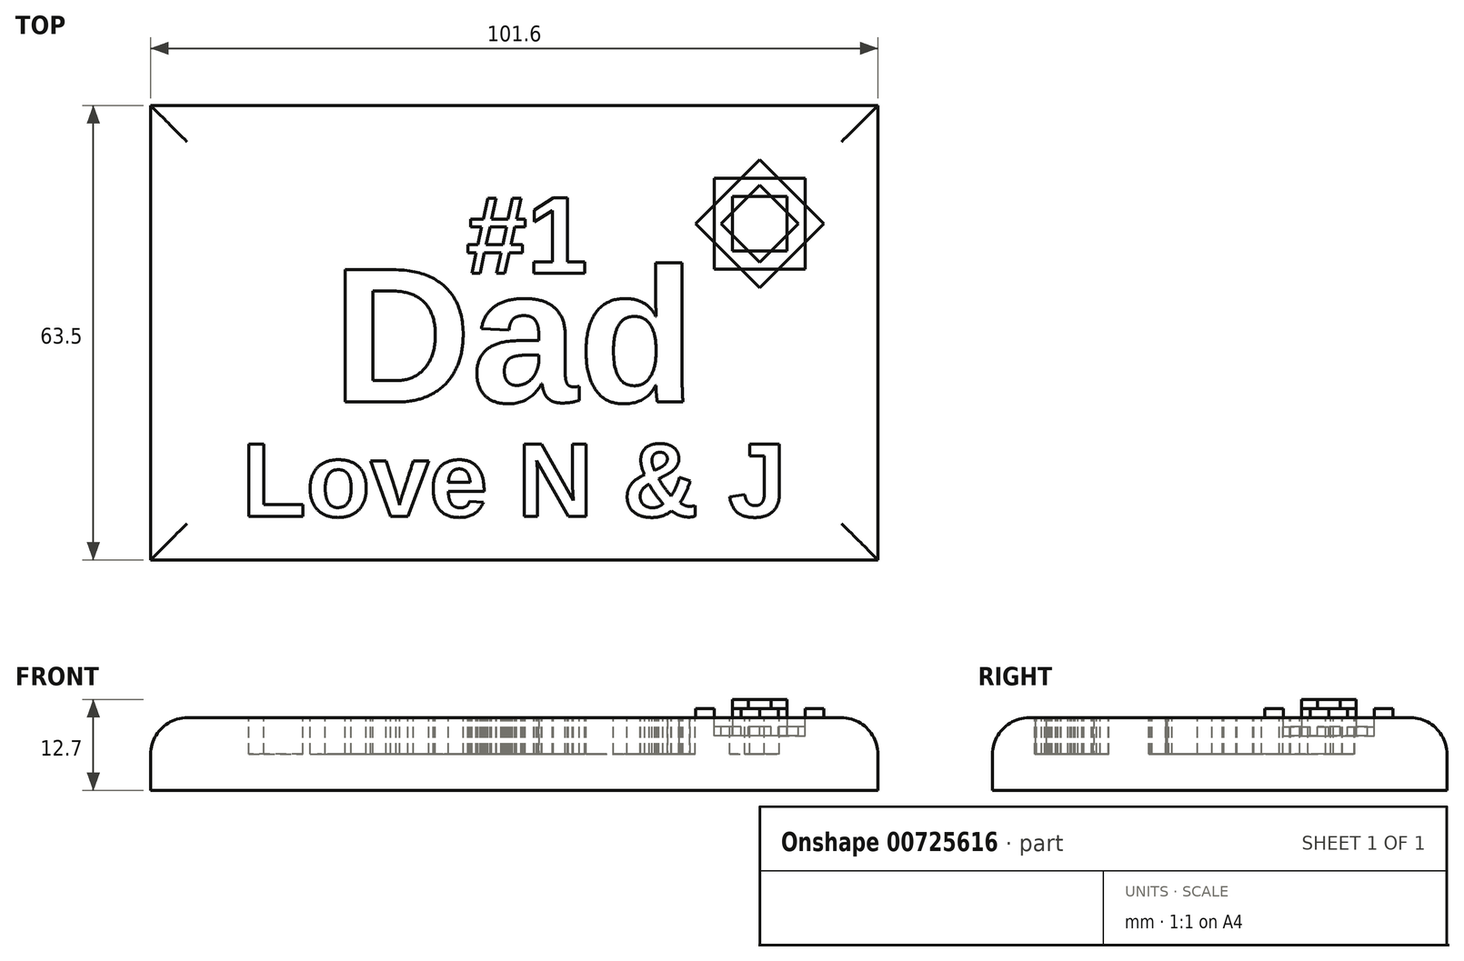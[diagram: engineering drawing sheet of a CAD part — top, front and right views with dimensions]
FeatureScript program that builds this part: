
annotation { "Feature Type Name" : "Feature", "Feature Type Description" : "" }
export const myFeature = defineFeature(function(context is Context, id is Id, definition is map)
    precondition{}
    {
        {
            var Q0;
            Q0=qCreatedBy(makeId("Top.planeOp"),FACE);
            var sketch = newSketch(context, id + "F0", { "sketchPlane" : qUnion([Q0])});
            skLineSegment(sketch, "E0.bottom", {"start": v(-50.8, 46.81) * mm, "end": v(50.8, 46.81) * mm});
            skLineSegment(sketch, "E0.top", {"start": v(-50.8, -16.69) * mm, "end": v(50.8, -16.69) * mm});
            skLineSegment(sketch, "E0.left", {"start": v(-50.8, 46.81) * mm, "end": v(-50.8, -16.69) * mm});
            skLineSegment(sketch, "E0.right", {"start": v(50.8, 46.81) * mm, "end": v(50.8, -16.69) * mm});
            skLineSegment(sketch, "E1", {"start": v(0, 46.81) * mm, "end": v(0, -16.69) * mm, "construction": true});
            skPoint(sketch, "E2", {"position": v(0, 15.06) * mm});
            skSolve(sketch);
        }
        {
            var Q0;
            Q0=qSketchRegion(id+"F0",true);
            extrude(context, id + "F1", {"entities" : qUnion([Q0]), "depth" : 10.16 * mm, "offsetDistance" : 25.4 * mm});
        }
        {
            var Q0;
            Q0=makeQuery(id+"F1.opExtrude","CAP_EDGE",EDGE,{"disambiguationData":[OSD([sQuery(id+"F0.wireOp",EDGE,"E0.left")])],"isStart":false});
            var Q1;
            Q1=makeQuery(id+"F1.opExtrude","CAP_EDGE",EDGE,{"disambiguationData":[OSD([sQuery(id+"F0.wireOp",EDGE,"E0.bottom")])],"isStart":false});
            var Q2;
            Q2=makeQuery(id+"F1.opExtrude","CAP_EDGE",EDGE,{"disambiguationData":[OSD([sQuery(id+"F0.wireOp",EDGE,"E0.right")])],"isStart":false});
            var Q3;
            Q3=makeQuery(id+"F1.opExtrude","CAP_EDGE",EDGE,{"disambiguationData":[OSD([sQuery(id+"F0.wireOp",EDGE,"E0.top")])],"isStart":false});
            fillet(context, id + "F2", {"entities" : qUnion([Q0, Q1, Q2, Q3]), "radius" : 5.08 * mm, "tangentPropagation" : true, "allowEdgeOverflow" : false});
        }
        {
            var Q0;
            Q0=makeQuery(id+"F1.opExtrude","CAP_FACE",FACE,{"disambiguationData":[OSD([sQuery(id+"F0.wireOp",EDGE,"E0.bottom"),sQuery(id+"F0.wireOp",EDGE,"E0.top"),sQuery(id+"F0.wireOp",EDGE,"E0.left"),sQuery(id+"F0.wireOp",EDGE,"E0.right")])],"isStart":false});
            var sketch = newSketch(context, id + "F3", { "sketchPlane" : qUnion([Q0])});
            skText(sketch, "E3", { "text": "Dad", "fontName": "Arimo-Bold.ttf"});
            skPoint(sketch, "E4", {"position": v(0, 15.06) * mm});
            skText(sketch, "E5", { "text": "#1", "fontName": "Arimo-Bold.ttf"});
            skText(sketch, "E6", { "text": "Love N & J", "fontName": "Arimo-Bold.ttf"});
            skPoint(sketch, "E7", {"position": v(0, -5.3) * mm});
            const initialGuessF3  = {"E3": [-0.0254, 0.0054, 1, 0, 0.01933], "E5": [-0.00674, 0.0234, 1, 0, 0.01102], "E6": [-0.0381, -0.01061, 1, 0, 0.01061]};
            skSetInitialGuess(sketch, initialGuessF3);
            skSolve(sketch);
        }
        {
            var Q0;
            Q0 = qSketchRegion(id + "F3", true);
            extrude(context, id + "F4", {"entities" : qUnion([Q0]), "operationType" : NewBodyOperationType.REMOVE, "oppositeDirection" : true, "depth" : 5.08 * mm, "offsetDistance" : 25.4 * mm});
        }
        {
            var Q0;
            {var subQ0=sQuery(id+"F0.wireOp",EDGE,"E0.right");var subQ1=sQuery(id+"F0.wireOp",EDGE,"E0.left");var subQ2=sQuery(id+"F0.wireOp",EDGE,"E0.top");var subQ3=sQuery(id+"F0.wireOp",EDGE,"E0.bottom");Q0=makeQuery(id+"F4.boolean.opBoolean","SPLIT",FACE,{"disambiguationData":[TD([makeQuery(id+"F2.opFillet","BLEND_FACE",FACE,{"disambiguationData":[OSD([subQ3])]})])],"derivedFrom":makeQuery(id+"F1.opExtrude","CAP_FACE",FACE,{"disambiguationData":[OSD([subQ3,subQ2,subQ1,subQ0])],"isStart":false})});}
            var sketch = newSketch(context, id + "F5", { "sketchPlane" : qUnion([Q0])});
            skLineSegment(sketch, "E8.bottom", {"start": v(40.64, 23.95) * mm, "end": v(27.94, 23.95) * mm});
            skLineSegment(sketch, "E8.top", {"start": v(40.64, 36.65) * mm, "end": v(27.94, 36.65) * mm});
            skLineSegment(sketch, "E8.left", {"start": v(40.64, 23.95) * mm, "end": v(40.64, 36.65) * mm});
            skLineSegment(sketch, "E8.right", {"start": v(27.94, 23.95) * mm, "end": v(27.94, 36.65) * mm});
            skPoint(sketch, "E8.middle", {"position": v(34.29, 30.3) * mm});
            skLineSegment(sketch, "E9.bottom", {"start": v(34.29, 21.32) * mm, "end": v(43.27, 30.3) * mm});
            skLineSegment(sketch, "E9.top", {"start": v(25.3, 30.3) * mm, "end": v(34.29, 39.28) * mm});
            skLineSegment(sketch, "E9.left", {"start": v(34.29, 21.32) * mm, "end": v(25.3, 30.3) * mm});
            skLineSegment(sketch, "E9.right", {"start": v(43.27, 30.3) * mm, "end": v(34.29, 39.28) * mm});
            skLineSegment(sketch, "E10.bottom", {"start": v(38.1, 34.11) * mm, "end": v(30.48, 34.11) * mm});
            skLineSegment(sketch, "E10.top", {"start": v(38.1, 26.5) * mm, "end": v(30.48, 26.5) * mm});
            skLineSegment(sketch, "E10.left", {"start": v(38.1, 34.11) * mm, "end": v(38.1, 26.5) * mm});
            skLineSegment(sketch, "E10.right", {"start": v(30.48, 34.11) * mm, "end": v(30.48, 26.5) * mm});
            skLineSegment(sketch, "E11.bottom", {"start": v(39.68, 30.3) * mm, "end": v(34.29, 35.7) * mm});
            skLineSegment(sketch, "E11.top", {"start": v(34.29, 24.92) * mm, "end": v(28.9, 30.3) * mm});
            skLineSegment(sketch, "E11.left", {"start": v(39.68, 30.3) * mm, "end": v(34.29, 24.92) * mm});
            skLineSegment(sketch, "E11.right", {"start": v(34.29, 35.7) * mm, "end": v(28.9, 30.3) * mm});
            skSolve(sketch);
        }
        {
            var Q0;
            {var subQ0=sQuery(id+"F5.wireOp",EDGE,"E9.right");var subQ1=sQuery(id+"F5.wireOp",EDGE,"E8.top");var subQ2=makeQuery(id+"F5.imprint","INTERSECT",VERTEX,{"derivedFrom":[subQ1,subQ0]});Q0=makeQuery(id+"F5.imprint","IMPRINT",FACE,{"disambiguationData":[TD([[makeQuery(id+"F5.imprint","IMPRINT",EDGE,{"disambiguationData":[TD([[subQ2,-1.0]])],"derivedFrom":subQ1}),-1.0]])]});}
            var Q1;
            {var subQ0=sQuery(id+"F5.wireOp",EDGE,"E9.left");var subQ1=sQuery(id+"F5.wireOp",EDGE,"E8.right");var subQ2=makeQuery(id+"F5.imprint","INTERSECT",VERTEX,{"derivedFrom":[subQ1,subQ0]});Q1=makeQuery(id+"F5.imprint","IMPRINT",FACE,{"disambiguationData":[TD([[makeQuery(id+"F5.imprint","IMPRINT",EDGE,{"disambiguationData":[TD([[subQ2,-1.0]])],"derivedFrom":subQ1}),1.0]])]});}
            var Q2;
            {var subQ0=sQuery(id+"F5.wireOp",EDGE,"E9.bottom");var subQ1=sQuery(id+"F5.wireOp",EDGE,"E8.bottom");var subQ2=makeQuery(id+"F5.imprint","INTERSECT",VERTEX,{"derivedFrom":[subQ1,subQ0]});Q2=makeQuery(id+"F5.imprint","IMPRINT",FACE,{"disambiguationData":[TD([[makeQuery(id+"F5.imprint","IMPRINT",EDGE,{"disambiguationData":[TD([[subQ2,-1.0]])],"derivedFrom":subQ1}),1.0]])]});}
            var Q3;
            {var subQ0=sQuery(id+"F5.wireOp",EDGE,"E9.bottom");var subQ1=sQuery(id+"F5.wireOp",EDGE,"E8.left");var subQ2=makeQuery(id+"F5.imprint","INTERSECT",VERTEX,{"derivedFrom":[subQ1,subQ0]});Q3=makeQuery(id+"F5.imprint","IMPRINT",FACE,{"disambiguationData":[TD([[makeQuery(id+"F5.imprint","IMPRINT",EDGE,{"disambiguationData":[TD([[subQ2,-1.0]])],"derivedFrom":subQ1}),-1.0]])]});}
            var Q4;
            {var subQ0=sQuery(id+"F5.wireOp",EDGE,"E10.left");var subQ1=sQuery(id+"F5.wireOp",EDGE,"E10.top");var subQ2=makeQuery(id+"F5.imprint","INTERSECT",VERTEX,{"derivedFrom":[subQ1,subQ0]});Q4=makeQuery(id+"F5.imprint","IMPRINT",FACE,{"disambiguationData":[TD([[makeQuery(id+"F5.imprint","IMPRINT",EDGE,{"disambiguationData":[TD([[subQ2,-1.0]])],"derivedFrom":subQ1}),-1.0]])]});}
            var Q5;
            {var subQ0=sQuery(id+"F5.wireOp",EDGE,"E10.right");var subQ1=sQuery(id+"F5.wireOp",EDGE,"E10.top");var subQ2=makeQuery(id+"F5.imprint","INTERSECT",VERTEX,{"derivedFrom":[subQ1,subQ0]});Q5=makeQuery(id+"F5.imprint","IMPRINT",FACE,{"disambiguationData":[TD([[makeQuery(id+"F5.imprint","IMPRINT",EDGE,{"disambiguationData":[TD([[subQ2,1.0]])],"derivedFrom":subQ1}),-1.0]])]});}
            var Q6;
            {var subQ0=sQuery(id+"F5.wireOp",EDGE,"E10.right");var subQ1=sQuery(id+"F5.wireOp",EDGE,"E10.bottom");var subQ2=makeQuery(id+"F5.imprint","INTERSECT",VERTEX,{"derivedFrom":[subQ1,subQ0]});Q6=makeQuery(id+"F5.imprint","IMPRINT",FACE,{"disambiguationData":[TD([[makeQuery(id+"F5.imprint","IMPRINT",EDGE,{"disambiguationData":[TD([[subQ2,1.0]])],"derivedFrom":subQ1}),1.0]])]});}
            var Q7;
            {var subQ0=sQuery(id+"F5.wireOp",EDGE,"E10.left");var subQ1=sQuery(id+"F5.wireOp",EDGE,"E10.bottom");var subQ2=makeQuery(id+"F5.imprint","INTERSECT",VERTEX,{"derivedFrom":[subQ1,subQ0]});Q7=makeQuery(id+"F5.imprint","IMPRINT",FACE,{"disambiguationData":[TD([[makeQuery(id+"F5.imprint","IMPRINT",EDGE,{"disambiguationData":[TD([[subQ2,-1.0]])],"derivedFrom":subQ1}),1.0]])]});}
            extrude(context, id + "F6", {"entities" : qUnion([Q0, Q1, Q2, Q3, Q4, Q5, Q6, Q7]), "operationType" : NewBodyOperationType.ADD, "depth" : 1.27 * mm, "offsetDistance" : 25.4 * mm});
        }
        {
            var Q0;
            {var subQ5=sQuery(id+"F5.wireOp",EDGE,"E11.bottom");var subQ13=sQuery(id+"F5.wireOp",EDGE,"E10.bottom");var subQ14=makeQuery(id+"F5.imprint","INTERSECT",VERTEX,{"derivedFrom":[subQ13,subQ5]});Q0=makeQuery(id+"F5.imprint","IMPRINT",FACE,{"disambiguationData":[TD([[makeQuery(id+"F5.imprint","IMPRINT",EDGE,{"disambiguationData":[TD([[subQ14,-1.0]])],"derivedFrom":subQ13}),1.0]])]});}
            extrude(context, id + "F7", {"entities" : qUnion([Q0]), "operationType" : NewBodyOperationType.ADD, "depth" : 2.54 * mm, "offsetDistance" : 25.4 * mm});
        }
        {
            var Q0;
            {var subQ0=sQuery(id+"F5.wireOp",EDGE,"E11.bottom");var subQ1=sQuery(id+"F5.wireOp",EDGE,"E10.bottom");var subQ2=makeQuery(id+"F5.imprint","INTERSECT",VERTEX,{"derivedFrom":[subQ1,subQ0]});Q0=makeQuery(id+"F5.imprint","IMPRINT",FACE,{"disambiguationData":[TD([[makeQuery(id+"F5.imprint","IMPRINT",EDGE,{"disambiguationData":[TD([[subQ2,-1.0]])],"derivedFrom":subQ1}),-1.0]])]});}
            var Q1;
            {var subQ0=sQuery(id+"F5.wireOp",EDGE,"E11.right");var subQ1=sQuery(id+"F5.wireOp",EDGE,"E10.right");var subQ2=makeQuery(id+"F5.imprint","INTERSECT",VERTEX,{"derivedFrom":[subQ1,subQ0]});Q1=makeQuery(id+"F5.imprint","IMPRINT",FACE,{"disambiguationData":[TD([[makeQuery(id+"F5.imprint","IMPRINT",EDGE,{"disambiguationData":[TD([[subQ2,-1.0]])],"derivedFrom":subQ1}),-1.0]])]});}
            var Q2;
            {var subQ0=sQuery(id+"F5.wireOp",EDGE,"E11.left");var subQ1=sQuery(id+"F5.wireOp",EDGE,"E10.top");var subQ2=makeQuery(id+"F5.imprint","INTERSECT",VERTEX,{"derivedFrom":[subQ1,subQ0]});Q2=makeQuery(id+"F5.imprint","IMPRINT",FACE,{"disambiguationData":[TD([[makeQuery(id+"F5.imprint","IMPRINT",EDGE,{"disambiguationData":[TD([[subQ2,-1.0]])],"derivedFrom":subQ1}),1.0]])]});}
            var Q3;
            {var subQ0=sQuery(id+"F5.wireOp",EDGE,"E11.bottom");var subQ1=sQuery(id+"F5.wireOp",EDGE,"E10.left");var subQ2=makeQuery(id+"F5.imprint","INTERSECT",VERTEX,{"derivedFrom":[subQ1,subQ0]});Q3=makeQuery(id+"F5.imprint","IMPRINT",FACE,{"disambiguationData":[TD([[makeQuery(id+"F5.imprint","IMPRINT",EDGE,{"disambiguationData":[TD([[subQ2,-1.0]])],"derivedFrom":subQ1}),1.0]])]});}
            var Q4;
            {var subQ0=sQuery(id+"F5.wireOp",EDGE,"E8.left");var subQ1=sQuery(id+"F5.wireOp",EDGE,"E8.top");var subQ2=makeQuery(id+"F5.imprint","INTERSECT",VERTEX,{"derivedFrom":[subQ1,subQ0]});Q4=makeQuery(id+"F5.imprint","IMPRINT",FACE,{"disambiguationData":[TD([[makeQuery(id+"F5.imprint","IMPRINT",EDGE,{"disambiguationData":[TD([[subQ2,-1.0]])],"derivedFrom":subQ1}),1.0]])]});}
            var Q5;
            {var subQ0=sQuery(id+"F5.wireOp",EDGE,"E8.right");var subQ1=sQuery(id+"F5.wireOp",EDGE,"E8.top");var subQ2=makeQuery(id+"F5.imprint","INTERSECT",VERTEX,{"derivedFrom":[subQ1,subQ0]});Q5=makeQuery(id+"F5.imprint","IMPRINT",FACE,{"disambiguationData":[TD([[makeQuery(id+"F5.imprint","IMPRINT",EDGE,{"disambiguationData":[TD([[subQ2,1.0]])],"derivedFrom":subQ1}),1.0]])]});}
            var Q6;
            {var subQ0=sQuery(id+"F5.wireOp",EDGE,"E8.right");var subQ1=sQuery(id+"F5.wireOp",EDGE,"E8.bottom");var subQ2=makeQuery(id+"F5.imprint","INTERSECT",VERTEX,{"derivedFrom":[subQ1,subQ0]});Q6=makeQuery(id+"F5.imprint","IMPRINT",FACE,{"disambiguationData":[TD([[makeQuery(id+"F5.imprint","IMPRINT",EDGE,{"disambiguationData":[TD([[subQ2,1.0]])],"derivedFrom":subQ1}),-1.0]])]});}
            var Q7;
            {var subQ0=sQuery(id+"F5.wireOp",EDGE,"E8.left");var subQ1=sQuery(id+"F5.wireOp",EDGE,"E8.bottom");var subQ2=makeQuery(id+"F5.imprint","INTERSECT",VERTEX,{"derivedFrom":[subQ1,subQ0]});Q7=makeQuery(id+"F5.imprint","IMPRINT",FACE,{"disambiguationData":[TD([[makeQuery(id+"F5.imprint","IMPRINT",EDGE,{"disambiguationData":[TD([[subQ2,-1.0]])],"derivedFrom":subQ1}),-1.0]])]});}
            extrude(context, id + "F8", {"entities" : qUnion([Q0, Q1, Q2, Q3, Q4, Q5, Q6, Q7]), "operationType" : NewBodyOperationType.REMOVE, "oppositeDirection" : true, "depth" : 1.27 * mm, "offsetDistance" : 25.4 * mm});
        }
        {
            var Q0;
            {var subQ27=sQuery(id+"F5.wireOp",EDGE,"E9.bottom");var subQ37=sQuery(id+"F5.wireOp",EDGE,"E8.bottom");var subQ38=makeQuery(id+"F5.imprint","INTERSECT",VERTEX,{"derivedFrom":[subQ37,subQ27]});Q0=makeQuery(id+"F5.imprint","IMPRINT",FACE,{"disambiguationData":[TD([[makeQuery(id+"F5.imprint","IMPRINT",EDGE,{"disambiguationData":[TD([[subQ38,-1.0]])],"derivedFrom":subQ37}),-1.0]])]});}
            extrude(context, id + "F9", {"entities" : qUnion([Q0]), "operationType" : NewBodyOperationType.REMOVE, "oppositeDirection" : true, "depth" : 2.54 * mm, "offsetDistance" : 25.4 * mm});
        }
    });
